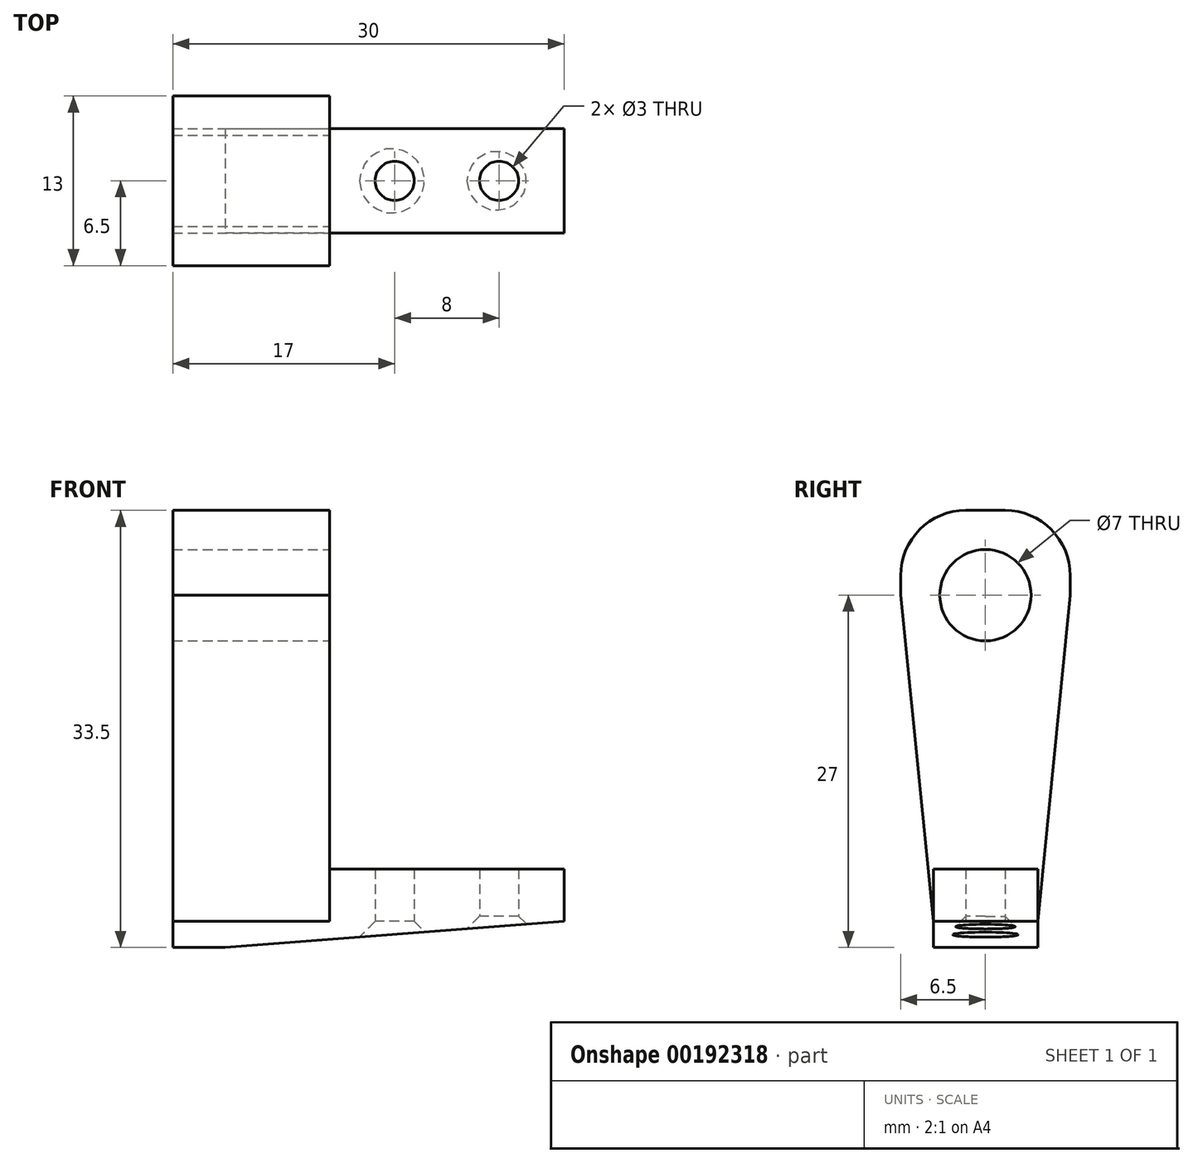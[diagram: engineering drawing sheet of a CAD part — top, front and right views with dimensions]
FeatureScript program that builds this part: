
annotation { "Feature Type Name" : "Feature", "Feature Type Description" : "" }
export const myFeature = defineFeature(function(context is Context, id is Id, definition is map)
    precondition{}
    {
        {
            var Q0;
            Q0=qCreatedBy(makeId("Top.planeOp"),FACE);
            var sketch = newSketch(context, id + "F0", { "sketchPlane" : qUnion([Q0])});
            skLineSegment(sketch, "E0.bottom", {"start": v(-15, -4) * mm, "end": v(15, -4) * mm});
            skLineSegment(sketch, "E0.top", {"start": v(-15, 4) * mm, "end": v(15, 4) * mm});
            skLineSegment(sketch, "E0.left", {"start": v(-15, -4) * mm, "end": v(-15, 4) * mm});
            skLineSegment(sketch, "E0.right", {"start": v(15, -4) * mm, "end": v(15, 4) * mm});
            skPoint(sketch, "E0.middle", {"position": v(0, 0) * mm});
            skLineSegment(sketch, "E1", {"start": v(-3, 4) * mm, "end": v(-3, -4) * mm});
            skLineSegment(sketch, "E2", {"start": v(-15, 0) * mm, "end": v(15, 0) * mm, "construction": true});
            skCircle(sketch, "E3", {"center": v(10, 0) * mm, "radius": 1.5 * mm});
            skCircle(sketch, "E4", {"center": v(2, 0) * mm, "radius": 1.5 * mm});
            skLineSegment(sketch, "E5", {"start": v(-15, 4) * mm, "end": v(-15, 6.5) * mm});
            skLineSegment(sketch, "E6", {"start": v(-15, 6.5) * mm, "end": v(-3, 6.5) * mm});
            skLineSegment(sketch, "E7", {"start": v(-3, 6.5) * mm, "end": v(-3, 4) * mm});
            skLineSegment(sketch, "E8.MirrorCS", {"start": v(-3, -6.5) * mm, "end": v(-3, -4) * mm});
            skLineSegment(sketch, "E9.MirrorCS", {"start": v(-15, -4) * mm, "end": v(-15, -6.5) * mm});
            skLineSegment(sketch, "E10.MirrorCS", {"start": v(-15, -6.5) * mm, "end": v(-3, -6.5) * mm});
            skSolve(sketch);
        }
        {
            var Q0;
            {var subQ1=sQuery(id+"F0.wireOp",EDGE,"E0.right");Q0=makeQuery(id+"F0.imprint","IMPRINT",FACE,{"disambiguationData":[TD([[makeQuery(id+"F0.imprint","IMPRINT",EDGE,{"derivedFrom":subQ1}),1.0]])]});}
            extrude(context, id + "F1", {"entities" : qUnion([Q0]), "depth" : 4 * mm});
        }
        {
            var Q0;
            {var subQ2=sQuery(id+"F0.wireOp",EDGE,"E8.MirrorCS");Q0=makeQuery(id+"F0.imprint","IMPRINT",FACE,{"disambiguationData":[TD([[makeQuery(id+"F0.imprint","IMPRINT",EDGE,{"derivedFrom":subQ2}),1.0]])]});}
            var Q1;
            {var subQ0=sQuery(id+"F0.wireOp",EDGE,"E0.left");Q1=makeQuery(id+"F0.imprint","IMPRINT",FACE,{"disambiguationData":[TD([[makeQuery(id+"F0.imprint","IMPRINT",EDGE,{"derivedFrom":subQ0}),-1.0]])]});}
            var Q2;
            {var subQ0=sQuery(id+"F0.wireOp",EDGE,"E5");Q2=makeQuery(id+"F0.imprint","IMPRINT",FACE,{"disambiguationData":[TD([[makeQuery(id+"F0.imprint","IMPRINT",EDGE,{"derivedFrom":subQ0}),-1.0]])]});}
            extrude(context, id + "F2", {"entities" : qUnion([Q0, Q1, Q2]), "operationType" : NewBodyOperationType.ADD, "depth" : 31.5 * mm});
        }
        {
            var Q0;
            Q0=makeQuery(id+"F2.opExtrude","SWEPT_FACE",FACE,{"disambiguationData":[OSD([sQuery(id+"F0.wireOp",EDGE,"E1"),sQuery(id+"F0.wireOp",EDGE,"E7"),sQuery(id+"F0.wireOp",EDGE,"E8.MirrorCS")])]});
            var sketch = newSketch(context, id + "F3", { "sketchPlane" : qUnion([Q0])});
            skLineSegment(sketch, "E11", {"start": v(0, 4) * mm, "end": v(0, 31.5) * mm, "construction": true});
            skLineSegment(sketch, "E12", {"start": v(-6.5, 25) * mm, "end": v(6.5, 25) * mm, "construction": true});
            skCircle(sketch, "E13", {"center": v(0, 25) * mm, "radius": 3.5 * mm});
            skLineSegment(sketch, "E14", {"start": v(-4, 0) * mm, "end": v(-6.5, 25) * mm});
            skLineSegment(sketch, "E15", {"start": v(6.5, 25) * mm, "end": v(4, 0) * mm});
            skSolve(sketch);
        }
        {
            var Q0;
            {var subQ0=sQuery(id+"F3.wireOp",EDGE,"E14");Q0=makeQuery(id+"F3.imprint","IMPRINT",FACE,{"disambiguationData":[TD([[makeQuery(id+"F3.imprint","IMPRINT",EDGE,{"derivedFrom":subQ0}),1.0]])]});}
            var Q1;
            {var subQ0=sQuery(id+"F3.wireOp",EDGE,"E15");Q1=makeQuery(id+"F3.imprint","IMPRINT",FACE,{"disambiguationData":[TD([[makeQuery(id+"F3.imprint","IMPRINT",EDGE,{"derivedFrom":subQ0}),1.0]])]});}
            var Q2;
            Q2=makeQuery(id+"F3.imprint","IMPRINT",FACE,{"disambiguationData":[TD([[makeQuery(id+"F3.imprint","IMPRINT",EDGE,{"derivedFrom":sQuery(id+"F3.wireOp",EDGE,"E13")}),1.0]])]});
            extrude(context, id + "F4", {"entities" : qUnion([Q0, Q1, Q2]), "operationType" : NewBodyOperationType.REMOVE, "endBound" : BoundingType.THROUGH_ALL, "oppositeDirection" : true, "depth" : 25 * mm});
        }
        {
            var Q0;
            Q0=makeQuery(id+"F2.opExtrude","CAP_EDGE",EDGE,{"disambiguationData":[OSD([sQuery(id+"F0.wireOp",EDGE,"E6")])],"isStart":false});
            var Q1;
            Q1=makeQuery(id+"F2.opExtrude","CAP_EDGE",EDGE,{"disambiguationData":[OSD([sQuery(id+"F0.wireOp",EDGE,"E10.MirrorCS")])],"isStart":false});
            fillet(context, id + "F5", {"entities" : qUnion([Q0, Q1]), "radius" : 5 * mm, "tangentPropagation" : true, "allowEdgeOverflow" : false});
        }
        {
            var Q0;
            {var subQ1=sQuery(id+"F0.wireOp",EDGE,"E0.right");Q0=makeQuery(id+"F0.imprint","IMPRINT",FACE,{"disambiguationData":[TD([[makeQuery(id+"F0.imprint","IMPRINT",EDGE,{"derivedFrom":subQ1}),1.0]])]});}
            var Q1;
            {var subQ0=sQuery(id+"F0.wireOp",EDGE,"E0.left");Q1=makeQuery(id+"F0.imprint","IMPRINT",FACE,{"disambiguationData":[TD([[makeQuery(id+"F0.imprint","IMPRINT",EDGE,{"derivedFrom":subQ0}),-1.0]])]});}
            extrude(context, id + "F6", {"entities" : qUnion([Q0, Q1]), "operationType" : NewBodyOperationType.ADD, "oppositeDirection" : true, "depth" : 2 * mm});
        }
        {
            var Q0;
            Q0=makeQuery(id+"F6.opExtrude","CAP_EDGE",EDGE,{"disambiguationData":[OSD([sQuery(id+"F0.wireOp",EDGE,"E4")])],"isStart":false});
            chamfer(context, id + "F7", {"entities" : qUnion([Q0]), "width" : 2 * mm, "tangentPropagation" : true});
        }
        {
            var Q0;
            Q0=makeQuery(id+"F6.opExtrude","CAP_EDGE",EDGE,{"disambiguationData":[OSD([sQuery(id+"F0.wireOp",EDGE,"E3")])],"isStart":false});
            chamfer(context, id + "F8", {"entities" : qUnion([Q0]), "width" : 2.4 * mm, "tangentPropagation" : true});
        }
        {
            var Q0;
            Q0=makeQuery(id+"F6.opExtrude","CAP_EDGE",EDGE,{"disambiguationData":[OSD([sQuery(id+"F0.wireOp",EDGE,"E0.right")])],"isStart":false});
            chamfer(context, id + "F9", {"entities" : qUnion([Q0]), "chamferType" : ChamferType.TWO_OFFSETS, "width1" : 2 * mm, "oppositeDirection" : false, "width2" : 26 * mm, "tangentPropagation" : true});
        }
    });
